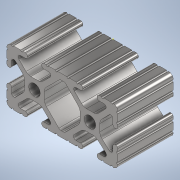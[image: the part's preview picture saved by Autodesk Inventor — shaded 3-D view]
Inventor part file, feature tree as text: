
AUTODESK INVENTOR PART (.ipt)
format: ipt  version: 2020 (Build 240168000, 168)  size: 347,136 bytes
history: native  units: in
note: dims shown in document units (in); Inventor stores cm internally (conversion verified against a paired STEP export)
features: sketch x2, extrude x1
ambient origin geometry x8: Origin, YZ Plane, XZ Plane, XY Plane, X Axis, Y Axis, Z Axis, Center Point
bodies: Solid1 (feature_tree)
feature tree (3):
  extrude  "Extrusion1"  [1 undecoded]
  sketch  "Sketch2"
  sketch  "Sketch1"  dims[d0=1.0in d1=0.0in]
note: 1 required parameter value undecoded (feature->parameter linkage not recoverable at this tier; creation-order binding heuristic only, values carry confidence <= 0.55)
